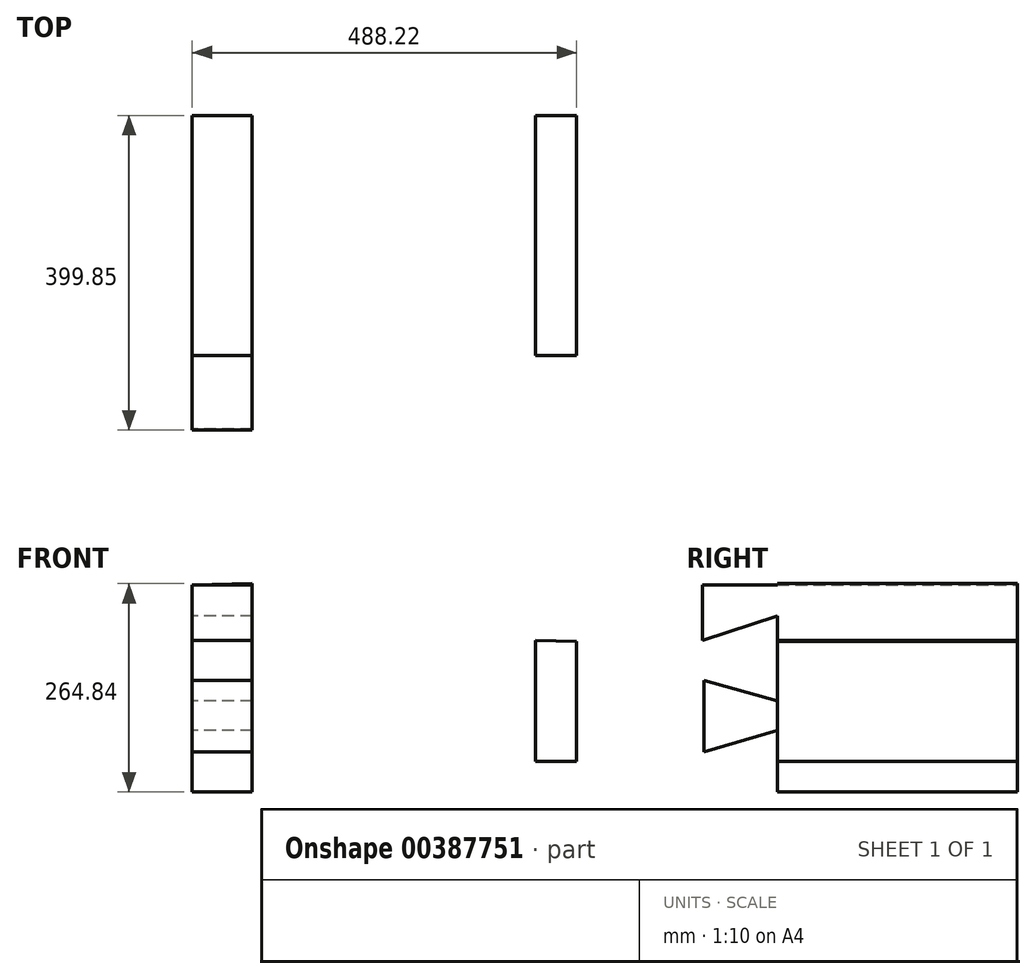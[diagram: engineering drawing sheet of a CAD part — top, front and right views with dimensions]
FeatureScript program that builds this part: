
annotation { "Feature Type Name" : "Feature", "Feature Type Description" : "" }
export const myFeature = defineFeature(function(context is Context, id is Id, definition is map)
    precondition{}
    {
        {
            var Q0;
            Q0=qCreatedBy(makeId("Front.planeOp"),FACE);
            var sketch = newSketch(context, id + "F0", { "sketchPlane" : qUnion([Q0])});
            skLineSegment(sketch, "E0", {"start": v(121.94, 76.8) * mm, "end": v(121.94, -76.62) * mm});
            skLineSegment(sketch, "E1", {"start": v(121.94, -76.62) * mm, "end": v(174, -76.62) * mm});
            skLineSegment(sketch, "E2", {"start": v(174, -76.62) * mm, "end": v(174, 75.78) * mm});
            skLineSegment(sketch, "E3", {"start": v(174, 75.78) * mm, "end": v(121.94, 76.8) * mm});
            skSolve(sketch);
        }
        {
            var Q0;
            Q0=makeQuery(id+"F0.imprint","IMPRINT",FACE,{"disambiguationData":[TD([[makeQuery(id+"F0.imprint","IMPRINT",EDGE,{"derivedFrom":sQuery(id+"F0.wireOp",EDGE,"E0")}),1.0]])]});
            extrude(context, id + "F1", {"entities" : qUnion([Q0]), "depth" : 304.8 * mm});
        }
        {
            var Q0;
            Q0=qCreatedBy(makeId("Front.planeOp"),FACE);
            var sketch = newSketch(context, id + "F2", { "sketchPlane" : qUnion([Q0])});
            skLineSegment(sketch, "E4", {"start": v(-314.22, 147.55) * mm, "end": v(-314.22, -115.84) * mm});
            skLineSegment(sketch, "E5", {"start": v(-314.22, -115.84) * mm, "end": v(-238.02, -115.84) * mm});
            skLineSegment(sketch, "E6", {"start": v(-238.02, -115.84) * mm, "end": v(-238.02, 149) * mm});
            skLineSegment(sketch, "E7", {"start": v(-238.02, 149) * mm, "end": v(-314.22, 147.55) * mm});
            skSolve(sketch);
        }
        {
            var Q0;
            Q0=makeQuery(id+"F2.imprint","IMPRINT",FACE,{"disambiguationData":[TD([[makeQuery(id+"F2.imprint","IMPRINT",EDGE,{"derivedFrom":sQuery(id+"F2.wireOp",EDGE,"E4")}),1.0]])]});
            extrude(context, id + "F3", {"entities" : qUnion([Q0]), "depth" : 304.8 * mm});
        }
        {
            var Q0;
            Q0=makeQuery(id+"F3.opExtrude","SWEPT_FACE",FACE,{"disambiguationData":[OSD([sQuery(id+"F2.wireOp",EDGE,"E4")])]});
            var sketch = newSketch(context, id + "F4", { "sketchPlane" : qUnion([Q0])});
            skLineSegment(sketch, "E8", {"start": v(304.8, 147.55) * mm, "end": v(399.85, 147.55) * mm});
            skLineSegment(sketch, "E9", {"start": v(399.85, 147.55) * mm, "end": v(399.85, 76.8) * mm});
            skLineSegment(sketch, "E10", {"start": v(399.85, 76.8) * mm, "end": v(304.8, 107.68) * mm});
            skLineSegment(sketch, "E11", {"start": v(304.8, 107.68) * mm, "end": v(304.8, 147.55) * mm});
            skSolve(sketch);
        }
        {
            var Q0;
            Q0=makeQuery(id+"F4.imprint","IMPRINT",FACE,{"disambiguationData":[TD([[makeQuery(id+"F4.imprint","IMPRINT",EDGE,{"derivedFrom":sQuery(id+"F4.wireOp",EDGE,"E8")}),-1.0]])]});
            var Q1;
            {var subQ2=sQuery(id+"F4.wireOp",EDGE,"E11");Q1=makeQuery(id+"F4.imprint","IMPRINT",FACE,{"disambiguationData":[TD([[makeQuery(id+"F4.imprint","IMPRINT",EDGE,{"derivedFrom":subQ2}),-1.0]])]});}
            extrude(context, id + "F5", {"entities" : qUnion([Q0, Q1]), "operationType" : NewBodyOperationType.ADD, "oppositeDirection" : true, "depth" : 76.2 * mm});
        }
        {
            var Q0;
            {var subQ0=sQuery(id+"F2.wireOp",EDGE,"E4");Q0=makeQuery(id+"F5.boolean.opBoolean","MERGE",FACE,{"derivedFrom":[makeQuery(id+"F3.opExtrude","SWEPT_FACE",FACE,{"disambiguationData":[OSD([subQ0])]}),makeQuery(id+"F5.opExtrude","CAP_FACE",FACE,{"disambiguationData":[OSD([subQ0,sQuery(id+"F2.wireOp",EDGE,"E5"),sQuery(id+"F2.wireOp",EDGE,"E7"),sQuery(id+"F4.wireOp",EDGE,"E8"),sQuery(id+"F4.wireOp",EDGE,"E9"),sQuery(id+"F4.wireOp",EDGE,"E10")])],"isStart":true})]});}
            var sketch = newSketch(context, id + "F6", { "sketchPlane" : qUnion([Q0])});
            skLineSegment(sketch, "E12", {"start": v(304.8, 0) * mm, "end": v(398.12, 26.15) * mm});
            skLineSegment(sketch, "E13", {"start": v(398.12, 26.15) * mm, "end": v(398.23, -64.47) * mm});
            skLineSegment(sketch, "E14", {"start": v(398.23, -64.47) * mm, "end": v(304.8, -37.4) * mm});
            skLineSegment(sketch, "E15", {"start": v(304.8, -37.4) * mm, "end": v(304.8, 0) * mm});
            skSolve(sketch);
        }
        {
            var Q0;
            Q0=makeQuery(id+"F6.imprint","IMPRINT",FACE,{"disambiguationData":[TD([[makeQuery(id+"F6.imprint","IMPRINT",EDGE,{"derivedFrom":sQuery(id+"F6.wireOp",EDGE,"E12")}),-1.0]])]});
            extrude(context, id + "F7", {"entities" : qUnion([Q0]), "operationType" : NewBodyOperationType.ADD, "oppositeDirection" : true, "depth" : 76.2 * mm});
        }
    });
